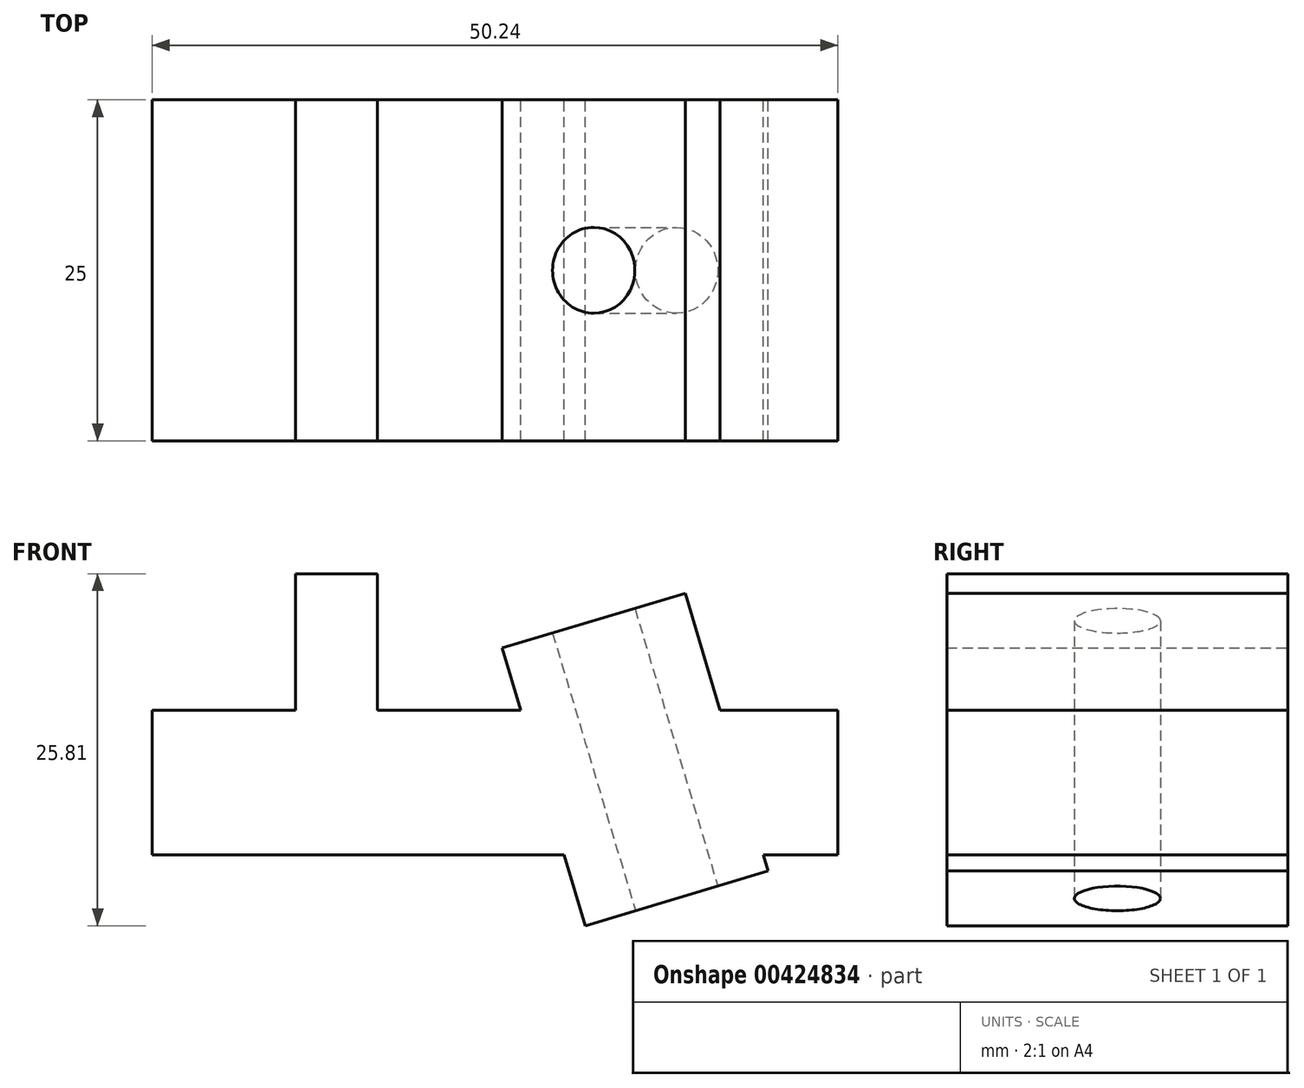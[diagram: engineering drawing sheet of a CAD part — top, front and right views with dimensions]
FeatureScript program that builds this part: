
annotation { "Feature Type Name" : "Feature", "Feature Type Description" : "" }
export const myFeature = defineFeature(function(context is Context, id is Id, definition is map)
    precondition{}
    {
        {
            var Q0;
            Q0=qCreatedBy(makeId("Front.planeOp"),FACE);
            var sketch = newSketch(context, id + "F0", { "sketchPlane" : qUnion([Q0])});
            skLineSegment(sketch, "E0.bottom", {"start": v(0, 0) * mm, "end": v(30.18, 0) * mm});
            skLineSegment(sketch, "E0.top", {"start": v(0, 10.63) * mm, "end": v(27, 10.63) * mm});
            skLineSegment(sketch, "E0.left", {"start": v(0, 0) * mm, "end": v(0, 10.63) * mm});
            skLineSegment(sketch, "E0.right", {"start": v(50.24, 0) * mm, "end": v(50.24, 10.63) * mm});
            skLineSegment(sketch, "E1", {"start": v(32.63, 16.26) * mm, "end": v(32.36, 17.18) * mm, "construction": true});
            skLineSegment(sketch, "E2.trimOffspring", {"start": v(41.62, 10.63) * mm, "end": v(50.24, 10.63) * mm});
            skLineSegment(sketch, "E3", {"start": v(25.65, 15.18) * mm, "end": v(31.73, -5.18) * mm});
            skLineSegment(sketch, "E4", {"start": v(25.65, 15.18) * mm, "end": v(32.36, 17.18) * mm});
            skLineSegment(sketch, "E5.MirrorCS", {"start": v(39.06, 19.18) * mm, "end": v(32.36, 17.18) * mm});
            skLineSegment(sketch, "E6.MirrorCS", {"start": v(39.06, 19.18) * mm, "end": v(45.14, -1.18) * mm});
            skLineSegment(sketch, "E7", {"start": v(31.73, -5.18) * mm, "end": v(45.14, -1.18) * mm});
            skLineSegment(sketch, "E8.trimOffspring", {"start": v(44.8, 0) * mm, "end": v(50.24, 0) * mm});
            skLineSegment(sketch, "E9", {"start": v(32.36, 17.18) * mm, "end": v(38.43, -3.18) * mm, "construction": true});
            skLineSegment(sketch, "E10", {"start": v(35.38, 18.08) * mm, "end": v(41.45, -2.28) * mm});
            skLineSegment(sketch, "E11", {"start": v(41.45, -2.28) * mm, "end": v(38.43, -3.18) * mm});
            skLineSegment(sketch, "E12", {"start": v(32.36, 17.18) * mm, "end": v(38.43, -3.18) * mm});
            skSolve(sketch);
        }
        {
            var Q0;
            {var subQ7=sQuery(id+"F0.wireOp",EDGE,"E10");Q0=makeQuery(id+"F0.imprint","IMPRINT",FACE,{"disambiguationData":[TD([[makeQuery(id+"F0.imprint","IMPRINT",EDGE,{"derivedFrom":subQ7}),1.0]])]});}
            var Q1;
            {var subQ0=sQuery(id+"F0.wireOp",EDGE,"E0.bottom");Q1=makeQuery(id+"F0.imprint","IMPRINT",FACE,{"disambiguationData":[TD([[makeQuery(id+"F0.imprint","IMPRINT",EDGE,{"derivedFrom":subQ0}),1.0]])]});}
            var Q2;
            {var subQ2=sQuery(id+"F0.wireOp",EDGE,"E10");Q2=makeQuery(id+"F0.imprint","IMPRINT",FACE,{"disambiguationData":[TD([[makeQuery(id+"F0.imprint","IMPRINT",EDGE,{"derivedFrom":subQ2}),-1.0]])]});}
            var Q3;
            Q3=makeQuery(id+"F0.imprint","IMPRINT",FACE,{"disambiguationData":[TD([[makeQuery(id+"F0.imprint","IMPRINT",EDGE,{"derivedFrom":sQuery(id+"F0.wireOp",EDGE,"E0.right")}),1.0]])]});
            var Q4;
            {var subQ0=sQuery(id+"F0.wireOp",EDGE,"E4");Q4=makeQuery(id+"F0.imprint","IMPRINT",FACE,{"disambiguationData":[TD([[makeQuery(id+"F0.imprint","IMPRINT",EDGE,{"derivedFrom":subQ0}),-1.0]])]});}
            extrude(context, id + "F1", {"entities" : qUnion([Q0, Q1, Q2, Q3, Q4]), "endBound" : BoundingType.SYMMETRIC, "depth" : 25 * mm});
        }
        {
            var Q0;
            {var subQ2=sQuery(id+"F0.wireOp",EDGE,"E10");Q0=makeQuery(id+"F0.imprint","IMPRINT",FACE,{"disambiguationData":[TD([[makeQuery(id+"F0.imprint","IMPRINT",EDGE,{"derivedFrom":subQ2}),-1.0]])]});}
            var Q1;
            Q1=sQuery(id+"F0.wireOp",EDGE,"E12");
            revolve(context, id + "F2", {"operationType" : NewBodyOperationType.REMOVE, "entities" : qUnion([Q0]), "axis" : qUnion([Q1]), "revolveType" : RevolveType.FULL, "oppositeDirection" : true});
        }
        {
            var Q0;
            Q0=makeQuery(id+"F1.opExtrude","SWEPT_FACE",FACE,{"disambiguationData":[OSD([sQuery(id+"F0.wireOp",EDGE,"E0.top")])]});
            var sketch = newSketch(context, id + "F3", { "sketchPlane" : qUnion([Q0])});
            skLineSegment(sketch, "E13.bottom", {"start": v(13.5, 12.5) * mm, "end": v(16.5, 12.5) * mm});
            skLineSegment(sketch, "E13.top", {"start": v(13.5, -12.5) * mm, "end": v(16.5, -12.5) * mm});
            skLineSegment(sketch, "E13.left", {"start": v(13.5, 12.5) * mm, "end": v(13.5, -12.5) * mm});
            skLineSegment(sketch, "E13.right", {"start": v(16.5, 12.5) * mm, "end": v(16.5, -12.5) * mm});
            skLineSegment(sketch, "E14.MirrorCS", {"start": v(10.5, 12.5) * mm, "end": v(10.5, -12.5) * mm});
            skLineSegment(sketch, "E15.MirrorCS", {"start": v(13.5, 12.5) * mm, "end": v(10.5, 12.5) * mm});
            skLineSegment(sketch, "E16.MirrorCS", {"start": v(13.5, -12.5) * mm, "end": v(10.5, -12.5) * mm});
            skSolve(sketch);
        }
        {
            var Q0;
            Q0=makeQuery(id+"F3.imprint","IMPRINT",FACE,{"disambiguationData":[TD([[makeQuery(id+"F3.imprint","IMPRINT",EDGE,{"derivedFrom":sQuery(id+"F3.wireOp",EDGE,"E13.bottom")}),-1.0]])]});
            var Q1;
            Q1=makeQuery(id+"F3.imprint","IMPRINT",FACE,{"disambiguationData":[TD([[makeQuery(id+"F3.imprint","IMPRINT",EDGE,{"derivedFrom":sQuery(id+"F3.wireOp",EDGE,"E13.left")}),-1.0]])]});
            extrude(context, id + "F4", {"entities" : qUnion([Q0, Q1]), "operationType" : NewBodyOperationType.ADD, "depth" : 10 * mm});
        }
    });
